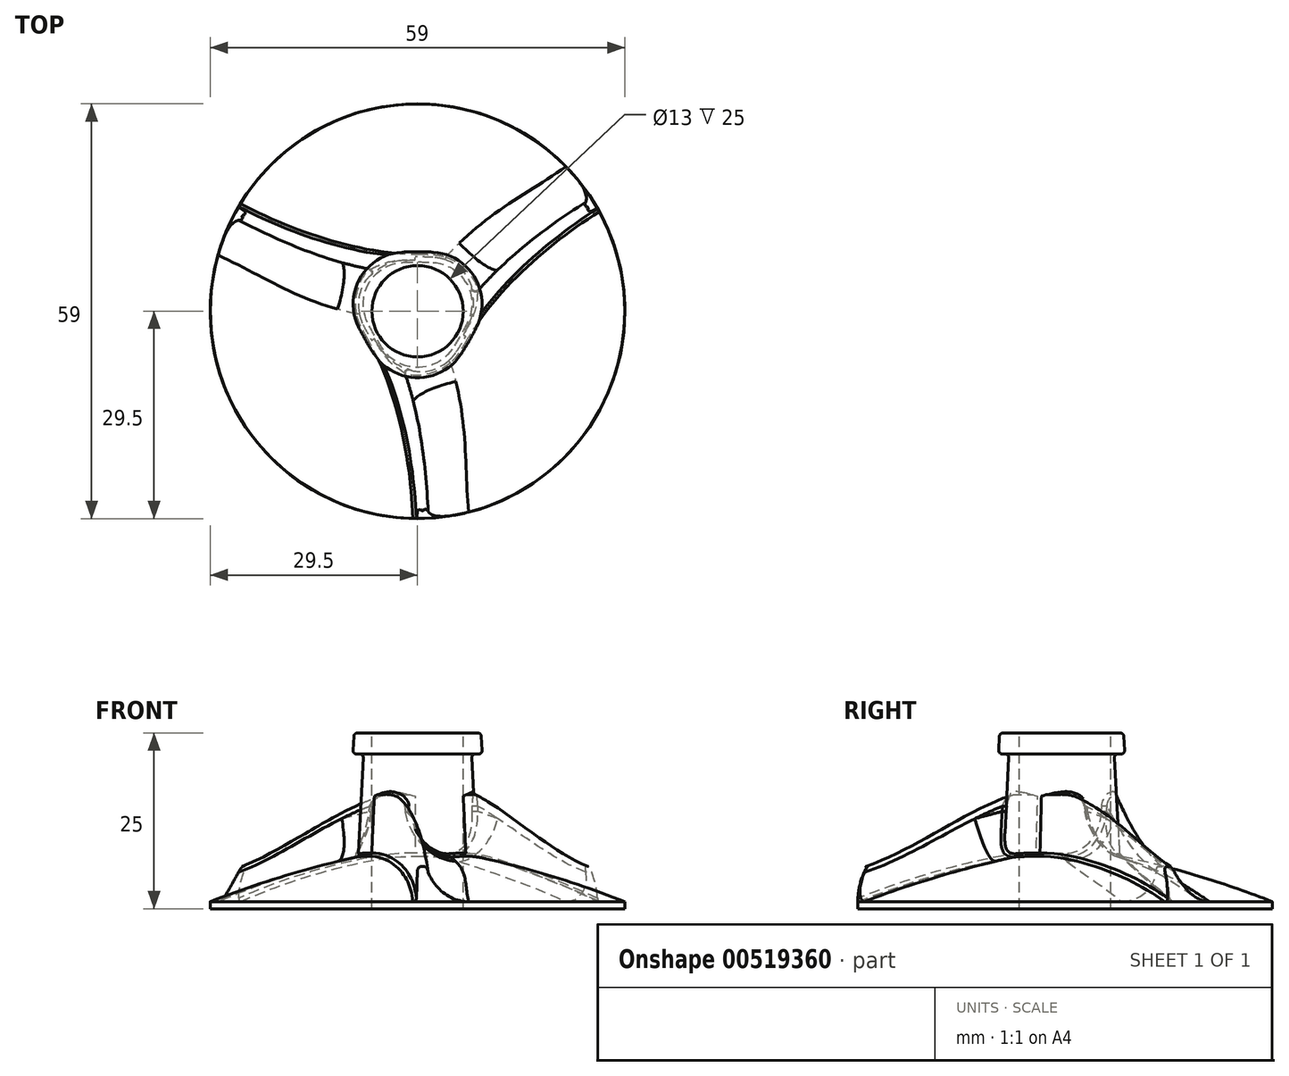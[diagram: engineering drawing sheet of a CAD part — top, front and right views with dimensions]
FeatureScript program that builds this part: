
annotation { "Feature Type Name" : "Feature", "Feature Type Description" : "" }
export const myFeature = defineFeature(function(context is Context, id is Id, definition is map)
    precondition{}
    {
        {
            var Q0;
            Q0=qCreatedBy(makeId("Front.planeOp"),FACE);
            var sketch = newSketch(context, id + "F0", { "sketchPlane" : qUnion([Q0])});
            skArc(sketch, "E0", {"start": v(0, 8) * mm, "mid": v(-14.97, 4.8) * mm, "end": v(-29.5, 0) * mm});
            skLineSegment(sketch, "E1", {"start": v(0, 0) * mm, "end": v(-29.5, 0) * mm});
            skLineSegment(sketch, "E2", {"start": v(0, 8) * mm, "end": v(0, 0) * mm});
            skSolve(sketch);
        }
        {
            var Q0;
            Q0 = qSketchRegion(id + "F0", true);
            var Q1;
            Q1=sQuery(id+"F0.wireOp",EDGE,"E2");
            revolve(context, id + "F1", {"entities" : qUnion([Q0]), "axis" : qUnion([Q1]), "revolveType" : RevolveType.FULL});
        }
        {
            var Q0;
            Q0=qCreatedBy(makeId("Top.planeOp"),FACE);
            var sketch = newSketch(context, id + "F2", { "sketchPlane" : qUnion([Q0])});
            skCircle(sketch, "E3.cCircle", {"center": v(0, 0) * mm, "radius": 6.33 * mm, "construction": true});
            skLineSegment(sketch, "E3.0", {"start": v(-10.97, 6.33) * mm, "end": v(10.97, 6.33) * mm, "construction": true});
            skLineSegment(sketch, "E3.1", {"start": v(10.97, 6.33) * mm, "end": v(0, -12.67) * mm, "construction": true});
            skLineSegment(sketch, "E3.2", {"start": v(0, -12.67) * mm, "end": v(-10.97, 6.33) * mm, "construction": true});
            skPoint(sketch, "E3.0.midPoint", {"position": v(0, 6.33) * mm});
            skArc(sketch, "E4", {"start": v(2.97, 8.7) * mm, "mid": v(0, 8.87) * mm, "end": v(-2.97, 8.7) * mm});
            skArc(sketch, "E5", {"start": v(-8.5, -1.19) * mm, "mid": v(-7.25, -3.63) * mm, "end": v(-5.82, -5.96) * mm});
            skArc(sketch, "E6", {"start": v(5.82, -5.96) * mm, "mid": v(7.25, -3.63) * mm, "end": v(8.5, -1.19) * mm});
            skPoint(sketch, "E7.visualSharp", {"position": v(-10.97, 6.33) * mm});
            skArc(sketch, "E7.filletArc", {"start": v(-2.97, 8.7) * mm, "mid": v(-8.24, 5.16) * mm, "end": v(-8.5, -1.19) * mm});
            skPoint(sketch, "E8.visualSharp", {"position": v(10.97, 6.33) * mm});
            skArc(sketch, "E8.filletArc", {"start": v(8.5, -1.19) * mm, "mid": v(8.24, 5.16) * mm, "end": v(2.97, 8.7) * mm});
            skPoint(sketch, "E9.visualSharp", {"position": v(0, -12.67) * mm});
            skArc(sketch, "E9.filletArc", {"start": v(-5.82, -5.96) * mm, "mid": v(0, -9.08) * mm, "end": v(5.82, -5.96) * mm});
            skLineSegment(sketch, "E10", {"start": v(0, 0) * mm, "end": v(-13.12, -7.57) * mm});
            skSolve(sketch);
        }
        {
            var Q0;
            Q0 = qSketchRegion(id + "F2", true);
            extrude(context, id + "F3", {"entities" : qUnion([Q0]), "operationType" : NewBodyOperationType.ADD, "depth" : 24 * mm, "offsetDistance" : 25 * mm, "hasDraft" : true, "draftAngle" : 3 * degree, "draftPullDirection" : true});
        }
        {
            var Q0;
            Q0=sQuery(id+"F2.wireOp",EDGE,"E10");
            cPlane(context, id + "F4", {"entities" : qUnion([Q0]), "cplaneType" : CPlaneType.LINE_ANGLE, "offset" : 25 * mm, "angle" : 0 * degree, "width" : 150 * mm, "height" : 150 * mm});
        }
        {
            var Q0;
            Q0=qCreatedBy(id+"F4.planeOp",FACE);
            var sketch = newSketch(context, id + "F5", { "sketchPlane" : qUnion([Q0])});
            skLineSegment(sketch, "E11.0.3", {"start": v(-6.7, 24) * mm, "end": v(-7.61, 6.45) * mm, "construction": true});
            skLineSegment(sketch, "E12", {"start": v(-7.3, 15) * mm, "end": v(-8.1, 0) * mm});
            skArc(sketch, "E13", {"start": v(-5.3, 15) * mm, "mid": v(-4.18, 7.4) * mm, "end": v(-2.1, 0) * mm});
            skLineSegment(sketch, "E14", {"start": v(-6.84, 24) * mm, "end": v(-7.75, 6.56) * mm, "construction": true});
            skLineSegment(sketch, "E15", {"start": v(-7.3, 15) * mm, "end": v(-5.3, 15) * mm, "construction": true});
            skLineSegment(sketch, "E16", {"start": v(-8.1, 0) * mm, "end": v(-2.1, 0) * mm});
            skArc(sketch, "E17", {"start": v(-10.1, 0) * mm, "mid": v(-8.2, 7.4) * mm, "end": v(-7.3, 15) * mm, "construction": true});
            skLineSegment(sketch, "E18", {"start": v(-10.1, 0) * mm, "end": v(-8.1, 0) * mm, "construction": true});
            skArc(sketch, "E19", {"start": v(-5.3, 15) * mm, "mid": v(-6.3, 15.95) * mm, "end": v(-7.3, 15) * mm});
            skSolve(sketch);
        }
        {
            var Q0;
            Q0=qCreatedBy(makeId("Top.planeOp"),FACE);
            var sketch = newSketch(context, id + "F6", { "sketchPlane" : qUnion([Q0])});
            skArc(sketch, "E20.0", {"start": v(-7, -4.05) * mm, "mid": v(-6.43, -5.01) * mm, "end": v(-5.82, -5.96) * mm, "construction": true});
            skCircle(sketch, "E21.0", {"center": v(0, 0) * mm, "radius": 29.5 * mm});
            skPoint(sketch, "E22.orphan", {"position": v(-8.5, -1.19) * mm});
            skPoint(sketch, "E23.orphan", {"position": v(-13.12, -7.57) * mm});
            skLineSegment(sketch, "E24.0", {"start": v(0, 0) * mm, "end": v(-13.12, -7.57) * mm, "construction": true});
            skSolve(sketch);
        }
        {
            var Q0;
            Q0=qCreatedBy(makeId("Top.planeOp"),FACE);
            var sketch = newSketch(context, id + "F7", { "sketchPlane" : qUnion([Q0])});
            skArc(sketch, "E25", {"start": v(0, -35) * mm, "mid": v(-1.16, -19) * mm, "end": v(-7, -4.05) * mm});
            skLineSegment(sketch, "E26", {"start": v(-7, -4.05) * mm, "end": v(-4.31, -8.72) * mm, "construction": true});
            skSolve(sketch);
        }
        {
            var Q0;
            Q0=sQuery(id+"F7.wireOp",VERTEX,"E25.start");
            var Q1;
            Q1=qCreatedBy(makeId("Front.planeOp"),FACE);
            cPlane(context, id + "F8", {"entities" : qUnion([Q0, Q1]), "cplaneType" : CPlaneType.PLANE_POINT, "offset" : 25 * mm, "width" : 150 * mm, "height" : 150 * mm});
        }
        {
            var Q0;
            Q0=qCreatedBy(id+"F8.planeOp",FACE);
            var sketch = newSketch(context, id + "F9", { "sketchPlane" : qUnion([Q0])});
            skLineSegment(sketch, "E27.0", {"start": v(0.14, 3) * mm, "end": v(0, 0) * mm});
            skArc(sketch, "E28.0", {"start": v(1.64, 3) * mm, "mid": v(2.29, 1.49) * mm, "end": v(3, 0) * mm});
            skLineSegment(sketch, "E29.0", {"start": v(-29.5, 0) * mm, "end": v(29.5, 0) * mm});
            skLineSegment(sketch, "E30", {"start": v(1.64, 3) * mm, "end": v(0.14, 3) * mm, "construction": true});
            skLineSegment(sketch, "E31", {"start": v(0, 0) * mm, "end": v(-0.5, 0) * mm, "construction": true});
            skLineSegment(sketch, "E32", {"start": v(-0.5, 0) * mm, "end": v(0.14, 3) * mm, "construction": true});
            skArc(sketch, "E33", {"start": v(1.64, 3) * mm, "mid": v(0.89, 3.72) * mm, "end": v(0.14, 3) * mm});
            skSolve(sketch);
        }
        {
            var Q1;
            {var subQ2=sQuery(id+"F9.wireOp",EDGE,"E28.0");Q1=makeQuery(id+"F9.imprint","IMPRINT",FACE,{"disambiguationData":[TD([[makeQuery(id+"F9.imprint","IMPRINT",EDGE,{"derivedFrom":subQ2}),-1.0]])]});}
            var Q2;
            Q2=makeQuery(id+"F5.imprint","IMPRINT",FACE,{"disambiguationData":[TD([[makeQuery(id+"F5.imprint","IMPRINT",EDGE,{"derivedFrom":sQuery(id+"F5.wireOp",EDGE,"E13")}),-1.0]])]});
            loft(context, id + "F10", {"startCondition" : LoftEndDerivativeType.NORMAL_TO_PROFILE, "startMagnitude" : 1, "endCondition" : LoftEndDerivativeType.NORMAL_TO_PROFILE, "endMagnitude" : 1, "sheetProfilesArray" : [{ "sheetProfileEntities" : qUnion([Q1]) }, { "sheetProfileEntities" : qUnion([Q2]) }]});
        }
        {
            var Q0;
            Q0=qCreatedBy(makeId("Top.planeOp"),FACE);
            var sketch = newSketch(context, id + "F11", { "sketchPlane" : qUnion([Q0])});
            skLineSegment(sketch, "E34", {"start": v(0, 0) * mm, "end": v(-25.55, -14.75) * mm});
            skLineSegment(sketch, "E35", {"start": v(25.55, -14.75) * mm, "end": v(0, 0) * mm});
            skArc(sketch, "E36.0", {"start": v(-25.55, -14.75) * mm, "mid": v(0, -29.5) * mm, "end": v(25.55, -14.75) * mm});
            skSolve(sketch);
        }
        {
            var Q0;
            Q0=makeQuery(id+"F3.opExtrude","CAP_FACE",FACE,{"disambiguationData":[OSD([sQuery(id+"F2.wireOp",EDGE,"E4"),sQuery(id+"F2.wireOp",EDGE,"E5"),sQuery(id+"F2.wireOp",EDGE,"E6"),sQuery(id+"F2.wireOp",EDGE,"E7.filletArc"),sQuery(id+"F2.wireOp",EDGE,"E8.filletArc"),sQuery(id+"F2.wireOp",EDGE,"E9.filletArc")])],"isStart":false});
            var sketch = newSketch(context, id + "F12", { "sketchPlane" : qUnion([Q0])});
            skArc(sketch, "E37.0", {"start": v(8.71, -1.29) * mm, "mid": v(8.45, 5.28) * mm, "end": v(3, 8.93) * mm});
            skArc(sketch, "E37.1", {"start": v(-3, 8.93) * mm, "mid": v(-8.45, 5.28) * mm, "end": v(-8.71, -1.29) * mm});
            skArc(sketch, "E37.2", {"start": v(-8.71, -1.29) * mm, "mid": v(-7.46, -3.74) * mm, "end": v(-6.03, -6.1) * mm});
            skArc(sketch, "E37.3", {"start": v(3, 8.93) * mm, "mid": v(0, 9.11) * mm, "end": v(-3, 8.93) * mm});
            skArc(sketch, "E37.4", {"start": v(-6.03, -6.1) * mm, "mid": v(0, -9.32) * mm, "end": v(6.03, -6.1) * mm});
            skArc(sketch, "E37.5", {"start": v(6.03, -6.1) * mm, "mid": v(7.46, -3.74) * mm, "end": v(8.71, -1.29) * mm});
            skSolve(sketch);
        }
        {
            var Q0;
            Q0 = qSketchRegion(id + "F12", true);
            extrude(context, id + "F13", {"entities" : qUnion([Q0]), "operationType" : NewBodyOperationType.ADD, "oppositeDirection" : true, "depth" : 3 * mm, "offsetDistance" : 25 * mm, "hasDraft" : true, "draftAngle" : 3 * degree});
        }
        {
            var Q0;
            Q0=makeQuery(id+"F13.boolean.opBoolean","MERGE",FACE,{"derivedFrom":[makeQuery(id+"F3.opExtrude","CAP_FACE",FACE,{"disambiguationData":[OSD([sQuery(id+"F2.wireOp",EDGE,"E4"),sQuery(id+"F2.wireOp",EDGE,"E5"),sQuery(id+"F2.wireOp",EDGE,"E6"),sQuery(id+"F2.wireOp",EDGE,"E7.filletArc"),sQuery(id+"F2.wireOp",EDGE,"E8.filletArc"),sQuery(id+"F2.wireOp",EDGE,"E9.filletArc")])],"isStart":false}),makeQuery(id+"F13.opExtrude","CAP_FACE",FACE,{"disambiguationData":[OSD([sQuery(id+"F12.wireOp",EDGE,"E37.0"),sQuery(id+"F12.wireOp",EDGE,"E37.1"),sQuery(id+"F12.wireOp",EDGE,"E37.2"),sQuery(id+"F12.wireOp",EDGE,"E37.3"),sQuery(id+"F12.wireOp",EDGE,"E37.4"),sQuery(id+"F12.wireOp",EDGE,"E37.5")])],"isStart":true})]});
            var sketch = newSketch(context, id + "F14", { "sketchPlane" : qUnion([Q0])});
            skCircle(sketch, "E38", {"center": v(0, 0) * mm, "radius": 6.5 * mm});
            skSolve(sketch);
        }
        {
            var Q0;
            Q0=makeQuery(id+"F11.imprint","IMPRINT",FACE,{"disambiguationData":[TD([[makeQuery(id+"F11.imprint","IMPRINT",EDGE,{"derivedFrom":sQuery(id+"F11.wireOp",EDGE,"E34")}),1.0]])]});
            extrude(context, id + "F15", {"entities" : qUnion([Q0]), "operationType" : NewBodyOperationType.INTERSECT, "depth" : 25 * mm, "offsetDistance" : 25 * mm});
        }
        {
            var Q0;
            {var subQ0=sQuery(id+"F9.wireOp",EDGE,"E27.0");Q0=makeQuery(id+"F10.opLoft","SWEPT_BODY",BODY,{"disambiguationData":[OSD([makeQuery(id+"F5.imprint","IMPRINT",FACE,{"disambiguationData":[TD([[makeQuery(id+"F5.imprint","IMPRINT",EDGE,{"derivedFrom":sQuery(id+"F5.wireOp",EDGE,"E12")}),1.0]])]}),makeQuery(id+"F9.imprint","IMPRINT",FACE,{"disambiguationData":[TD([[makeQuery(id+"F9.imprint","IMPRINT",EDGE,{"derivedFrom":subQ0}),1.0]])]})])]});}
            var Q1;
            Q1=makeQuery(id+"F1.opRevolve","SWEPT_BODY",BODY,{"disambiguationData":[OSD([sQuery(id+"F0.wireOp",EDGE,"E0"),sQuery(id+"F0.wireOp",EDGE,"E1"),sQuery(id+"F0.wireOp",EDGE,"E2")])]});
            booleanBodies(context, id + "F16", {"operationType" : BooleanOperationType.UNION, "tools" : qUnion([Q0, Q1])});
        }
        {
            var Q0;
            Q0=makeQuery(id+"F16.opBoolean","INTERSECT",EDGE,{"derivedFrom":[makeQuery(id+"F1.opRevolve","SWEPT_FACE",FACE,{"disambiguationData":[OSD([sQuery(id+"F0.wireOp",EDGE,"E0")])]}),makeQuery(id+"F10.opLoft","SWEPT_FACE",FACE,{"disambiguationData":[OSD([sQuery(id+"F5.wireOp",EDGE,"E13"),sQuery(id+"F5.wireOp",EDGE,"E16"),sQuery(id+"F5.wireOp",EDGE,"E19"),sQuery(id+"F9.wireOp",EDGE,"E28.0"),sQuery(id+"F9.wireOp",EDGE,"E29.0"),sQuery(id+"F9.wireOp",EDGE,"E33")])]})]});
            fillet(context, id + "F17", {"entities" : qUnion([Q0]), "radius" : 7 * mm, "tangentPropagation" : true, "allowEdgeOverflow" : false});
        }
        {
            var Q0;
            Q0=makeQuery(id+"F17.opFillet","BLEND_EDGE",EDGE,{"blendedFrom":[makeQuery(id+"F16.opBoolean","INTERSECT",EDGE,{"derivedFrom":[makeQuery(id+"F1.opRevolve","SWEPT_FACE",FACE,{"disambiguationData":[OSD([sQuery(id+"F0.wireOp",EDGE,"E0")])]}),makeQuery(id+"F10.opLoft","SWEPT_FACE",FACE,{"disambiguationData":[OSD([sQuery(id+"F5.wireOp",EDGE,"E13"),sQuery(id+"F5.wireOp",EDGE,"E16"),sQuery(id+"F5.wireOp",EDGE,"E19"),sQuery(id+"F9.wireOp",EDGE,"E28.0"),sQuery(id+"F9.wireOp",EDGE,"E29.0"),sQuery(id+"F9.wireOp",EDGE,"E33")])]})]}),makeQuery(id+"F3.opExtrude","SWEPT_FACE",FACE,{"disambiguationData":[OSD([sQuery(id+"F2.wireOp",EDGE,"E9.filletArc")])]})],"blendedInto":[makeQuery(id+"F3.opExtrude","SWEPT_FACE",FACE,{"disambiguationData":[OSD([sQuery(id+"F2.wireOp",EDGE,"E9.filletArc")])]})]});
            var Q1;
            Q1=makeQuery(id+"F16.opBoolean","INTERSECT",EDGE,{"derivedFrom":[makeQuery(id+"F1.opRevolve","SWEPT_FACE",FACE,{"disambiguationData":[OSD([sQuery(id+"F0.wireOp",EDGE,"E0")])]}),makeQuery(id+"F10.opLoft","SWEPT_FACE",FACE,{"disambiguationData":[OSD([sQuery(id+"F5.wireOp",EDGE,"E12"),sQuery(id+"F5.wireOp",EDGE,"E13"),sQuery(id+"F5.wireOp",EDGE,"E16"),sQuery(id+"F5.wireOp",EDGE,"E19"),sQuery(id+"F9.wireOp",EDGE,"E27.0"),sQuery(id+"F9.wireOp",EDGE,"E28.0"),sQuery(id+"F9.wireOp",EDGE,"E29.0"),sQuery(id+"F9.wireOp",EDGE,"E33")])]})]});
            var Q2;
            Q2=makeQuery(id+"F13.opExtrude","CAP_EDGE",EDGE,{"disambiguationData":[OSD([sQuery(id+"F12.wireOp",EDGE,"E37.4")])],"isStart":true});
            var Q3;
            Q3=makeQuery(id+"F13.opExtrude","CAP_EDGE",EDGE,{"disambiguationData":[OSD([sQuery(id+"F12.wireOp",EDGE,"E37.4")])],"isStart":false});
            var Q4;
            Q4=makeQuery(id+"F13.boolean.opBoolean","INTERSECT",EDGE,{"derivedFrom":[makeQuery(id+"F3.opExtrude","SWEPT_FACE",FACE,{"disambiguationData":[OSD([sQuery(id+"F2.wireOp",EDGE,"E5")])]}),makeQuery(id+"F13.opExtrude","CAP_FACE",FACE,{"disambiguationData":[OSD([sQuery(id+"F12.wireOp",EDGE,"E37.0"),sQuery(id+"F12.wireOp",EDGE,"E37.1"),sQuery(id+"F12.wireOp",EDGE,"E37.2"),sQuery(id+"F12.wireOp",EDGE,"E37.3"),sQuery(id+"F12.wireOp",EDGE,"E37.4"),sQuery(id+"F12.wireOp",EDGE,"E37.5")])],"isStart":false})]});
            fillet(context, id + "F18", {"entities" : qUnion([Q0, Q1, Q2, Q3, Q4]), "radius" : 0.5 * mm, "tangentPropagation" : true, "allowEdgeOverflow" : false});
        }
        {
            var Q0;
            {var subQ0=sQuery(id+"F9.wireOp",EDGE,"E27.0");Q0=makeQuery(id+"F10.opLoft","SWEPT_BODY",BODY,{"disambiguationData":[OSD([makeQuery(id+"F5.imprint","IMPRINT",FACE,{"disambiguationData":[TD([[makeQuery(id+"F5.imprint","IMPRINT",EDGE,{"derivedFrom":sQuery(id+"F5.wireOp",EDGE,"E12")}),1.0]])]}),makeQuery(id+"F9.imprint","IMPRINT",FACE,{"disambiguationData":[TD([[makeQuery(id+"F9.imprint","IMPRINT",EDGE,{"derivedFrom":subQ0}),1.0]])]})])]});}
            var Q1;
            Q1=sQuery(id+"F0.wireOp",EDGE,"E2");
            circularPattern(context, id + "F19", {"operationType" : NewBodyOperationType.ADD, "entities" : qUnion([Q0]), "axis" : qUnion([Q1]), "angle" : 360 * degree, "instanceCount" : 3, "equalSpace" : true});
        }
        {
            var Q0;
            Q0 = qSketchRegion(id + "F14", true);
            extrude(context, id + "F20", {"entities" : qUnion([Q0]), "operationType" : NewBodyOperationType.REMOVE, "endBound" : BoundingType.THROUGH_ALL, "oppositeDirection" : true, "depth" : 25 * mm, "offsetDistance" : 25 * mm});
        }
        {
            var Q0;
            Q0=qCreatedBy(makeId("Right.planeOp"),FACE);
            var sketch = newSketch(context, id + "F21", { "sketchPlane" : qUnion([Q0])});
            skArc(sketch, "E39", {"start": v(-28.15, 5) * mm, "mid": v(-29.15, 2.59) * mm, "end": v(-29.5, 0) * mm});
            skLineSegment(sketch, "E40.0.0", {"start": v(-29.5, 0) * mm, "end": v(-28.59, 0) * mm, "construction": true});
            skFitSpline(sketch, "E40.0.5", {"points": [v(-29.5, 0.5) * mm, v(-29.5, 0.43) * mm, v(-29.5, 0.3) * mm, v(-29.5, 0.08) * mm, v(-29.5, 0) * mm, v(-29.5, 0) * mm], "construction": true});
            skLineSegment(sketch, "E41", {"start": v(-28.15, 5) * mm, "end": v(-29.5, 5) * mm});
            skLineSegment(sketch, "E42", {"start": v(-29.5, 5) * mm, "end": v(-29.5, 0) * mm, "construction": true});
            skLineSegment(sketch, "E43", {"start": v(0, 0) * mm, "end": v(0, 40.82) * mm});
            skLineSegment(sketch, "E44", {"start": v(-29.5, 5) * mm, "end": v(-30.8, 5) * mm});
            skLineSegment(sketch, "E45", {"start": v(-30.8, 5) * mm, "end": v(-30.8, 0) * mm});
            skLineSegment(sketch, "E46", {"start": v(-30.8, 0) * mm, "end": v(-29.5, 0) * mm});
            skSolve(sketch);
        }
        {
            var Q0;
            Q0=makeQuery(id+"F6.imprint","IMPRINT",FACE,{"disambiguationData":[TD([[makeQuery(id+"F6.imprint","IMPRINT",EDGE,{"derivedFrom":sQuery(id+"F6.wireOp",EDGE,"E21.0")}),1.0]])]});
            var sketch = newSketch(context, id + "F22", { "sketchPlane" : qUnion([Q0])});
            skCircle(sketch, "E47.0.0", {"center": v(0, 0) * mm, "radius": 29.5 * mm});
            skCircle(sketch, "E48.0", {"center": v(0, 0) * mm, "radius": 6.5 * mm});
            skSolve(sketch);
        }
        {
            var Q0;
            Q0 = qSketchRegion(id + "F22", true);
            extrude(context, id + "F23", {"entities" : qUnion([Q0]), "operationType" : NewBodyOperationType.ADD, "oppositeDirection" : true, "depth" : 1 * mm, "offsetDistance" : 25 * mm});
        }
        {
            var Q0;
            Q0 = qSketchRegion(id + "F21", true);
            var Q1;
            Q1=sQuery(id+"F21.wireOp",EDGE,"E43");
            revolve(context, id + "F24", {"operationType" : NewBodyOperationType.REMOVE, "entities" : qUnion([Q0]), "axis" : qUnion([Q1]), "revolveType" : RevolveType.FULL, "oppositeDirection" : true});
        }
    });
